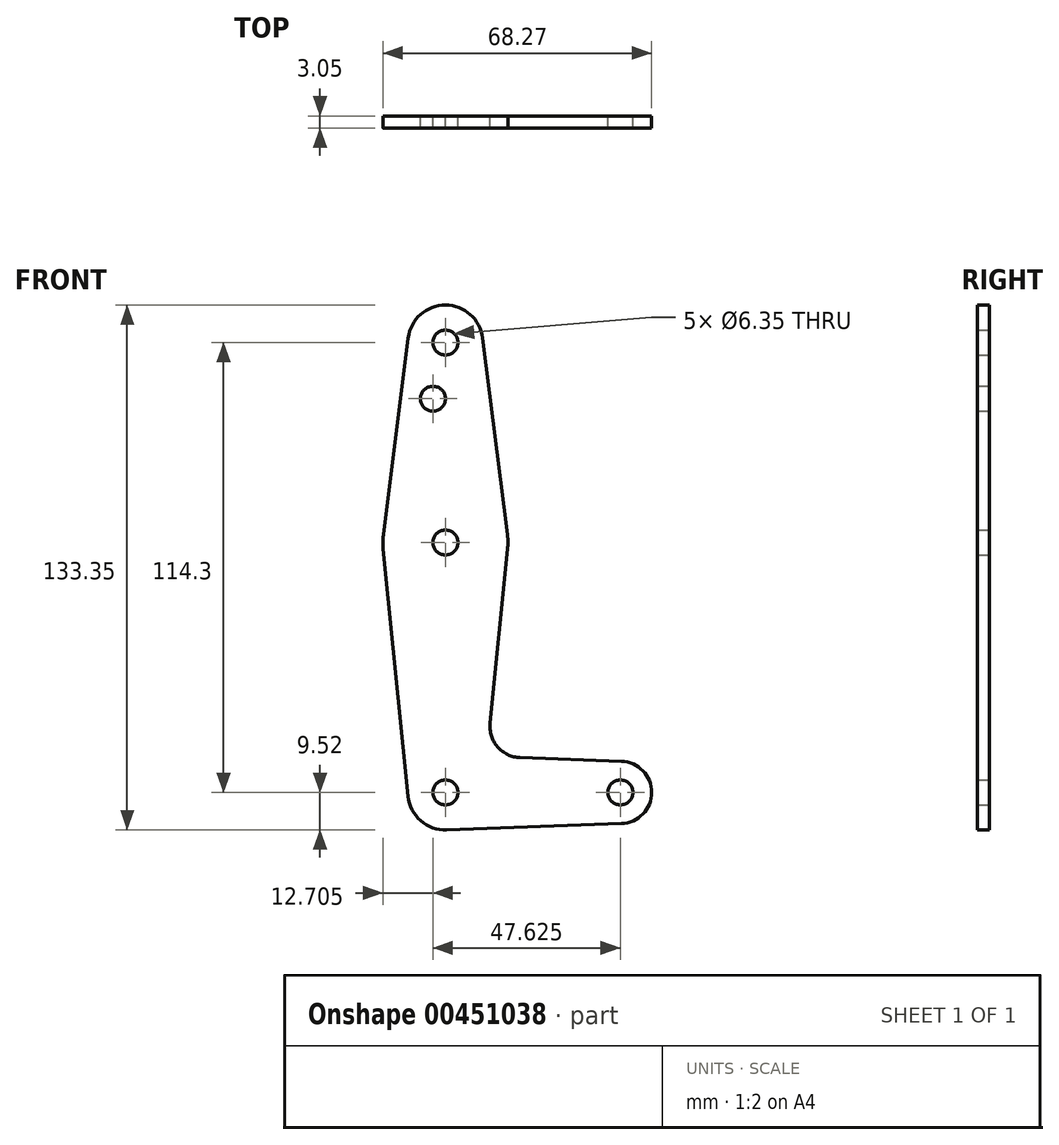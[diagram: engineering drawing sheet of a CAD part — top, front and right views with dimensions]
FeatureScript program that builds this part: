
annotation { "Feature Type Name" : "Feature", "Feature Type Description" : "" }
export const myFeature = defineFeature(function(context is Context, id is Id, definition is map)
    precondition{}
    {
        {
            var Q0;
            Q0=qCreatedBy(makeId("Front.planeOp"),FACE);
            var sketch = newSketch(context, id + "F0", { "sketchPlane" : qUnion([Q0])});
            skLineSegment(sketch, "E0", {"start": v(0, 114.3) * mm, "end": v(0, 0) * mm, "construction": true});
            skLineSegment(sketch, "E1", {"start": v(0, 0) * mm, "end": v(44.45, 0) * mm, "construction": true});
            skCircle(sketch, "E2", {"center": v(0, 114.3) * mm, "radius": 9.52 * mm});
            skCircle(sketch, "E3", {"center": v(0, 63.5) * mm, "radius": 15.88 * mm});
            skCircle(sketch, "E4", {"center": v(0, 0) * mm, "radius": 9.53 * mm});
            skCircle(sketch, "E5", {"center": v(44.45, 0) * mm, "radius": 7.94 * mm});
            skLineSegment(sketch, "E6", {"start": v(9.45, 115.5) * mm, "end": v(15.75, 65.48) * mm});
            skLineSegment(sketch, "E7", {"start": v(-15.75, 65.48) * mm, "end": v(-9.45, 115.5) * mm});
            skLineSegment(sketch, "E8", {"start": v(-15.8, 61.91) * mm, "end": v(-9.48, -0.95) * mm});
            skLineSegment(sketch, "E9", {"start": v(15.8, 61.91) * mm, "end": v(11.34, 17.6) * mm});
            skLineSegment(sketch, "E10", {"start": v(0.34, -9.52) * mm, "end": v(44.73, -7.93) * mm});
            skLineSegment(sketch, "E11", {"start": v(18.97, 8.85) * mm, "end": v(44.73, 7.93) * mm});
            skCircle(sketch, "E12", {"center": v(0, 114.3) * mm, "radius": 3.18 * mm});
            skCircle(sketch, "E13", {"center": v(0, 63.5) * mm, "radius": 3.18 * mm});
            skCircle(sketch, "E14", {"center": v(0, 0) * mm, "radius": 3.18 * mm});
            skCircle(sketch, "E15", {"center": v(44.45, 0) * mm, "radius": 3.18 * mm});
            skCircle(sketch, "E16", {"center": v(-3.17, 100.03) * mm, "radius": 3.18 * mm});
            skArc(sketch, "E17.filletArc", {"start": v(11.34, 17.6) * mm, "mid": v(13.26, 11.57) * mm, "end": v(18.97, 8.85) * mm});
            skSolve(sketch);
        }
        {
            var Q0;
            Q0 = qSketchRegion(id + "F0", true);
            extrude(context, id + "F1", {"entities" : qUnion([Q0]), "depth" : 3.05 * mm});
        }
    });
